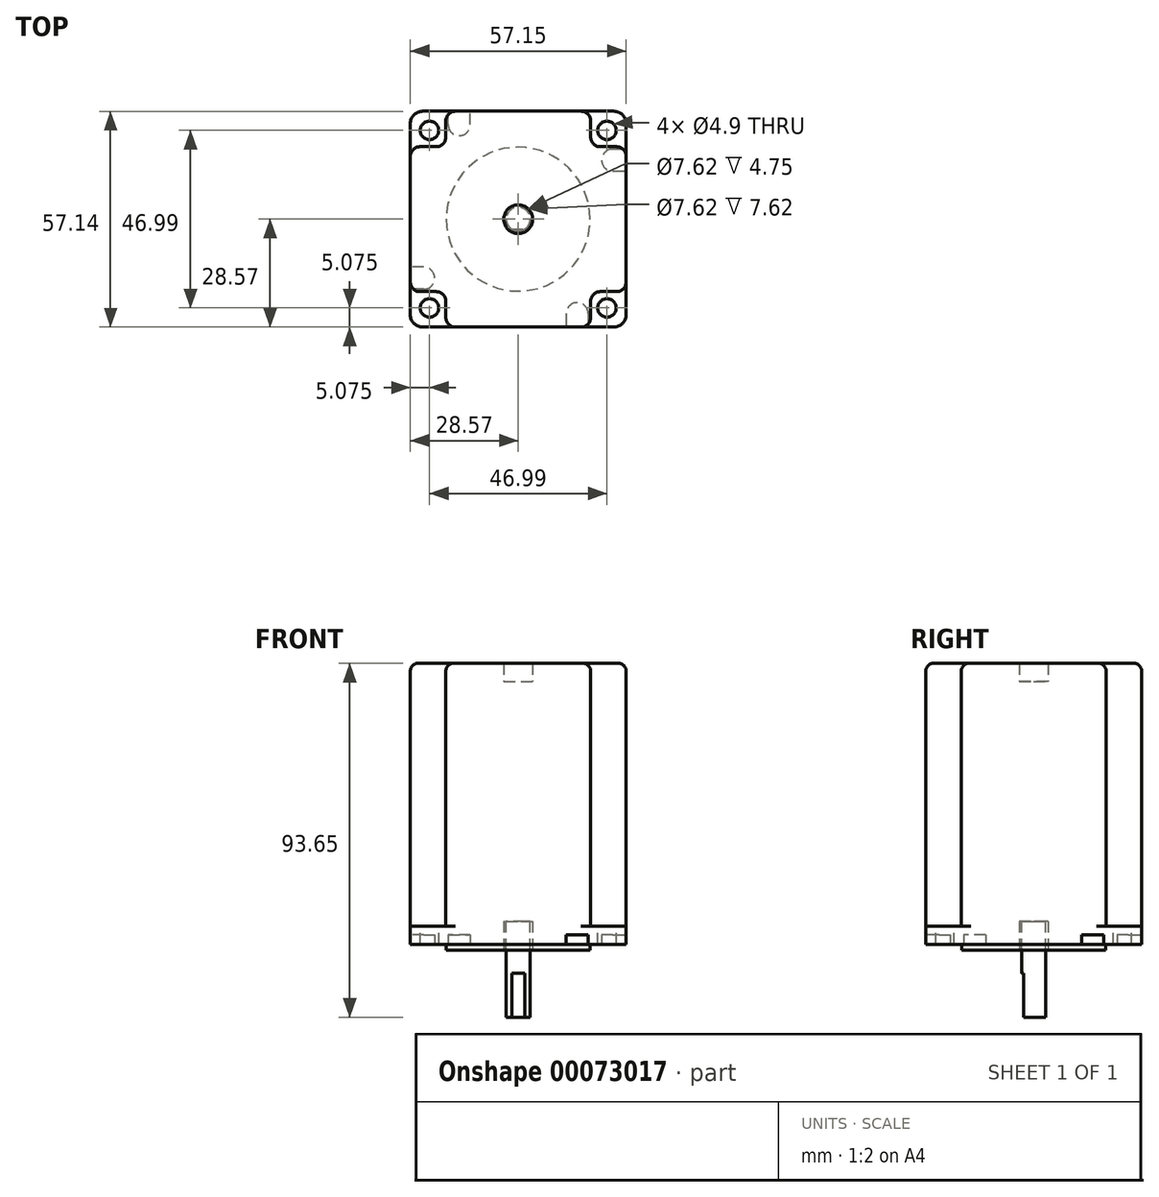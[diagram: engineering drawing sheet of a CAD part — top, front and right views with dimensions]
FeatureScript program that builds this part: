
annotation { "Feature Type Name" : "Feature", "Feature Type Description" : "" }
export const myFeature = defineFeature(function(context is Context, id is Id, definition is map)
    precondition{}
    {
        {
            var Q0;
            Q0=qCreatedBy(makeId("Top.planeOp"),FACE);
            var sketch = newSketch(context, id + "F0", { "sketchPlane" : qUnion([Q0])});
            skLineSegment(sketch, "E0.bottom", {"start": v(-25.27, 28.58) * mm, "end": v(25.27, 28.58) * mm});
            skLineSegment(sketch, "E0.top", {"start": v(-25.27, -28.58) * mm, "end": v(25.27, -28.58) * mm});
            skLineSegment(sketch, "E0.left", {"start": v(-28.57, 25.27) * mm, "end": v(-28.58, -25.27) * mm});
            skLineSegment(sketch, "E0.right", {"start": v(28.58, 25.27) * mm, "end": v(28.57, -25.27) * mm});
            skPoint(sketch, "E0.middle", {"position": v(0, 0) * mm});
            skCircle(sketch, "E1", {"center": v(-23.5, 23.5) * mm, "radius": 2.45 * mm});
            skPoint(sketch, "E2.visualSharp", {"position": v(-28.57, 28.58) * mm});
            skArc(sketch, "E2.filletArc", {"start": v(-25.27, 28.58) * mm, "mid": v(-27.6, 27.6) * mm, "end": v(-28.57, 25.27) * mm});
            skPoint(sketch, "E3.visualSharp", {"position": v(28.58, 28.58) * mm});
            skArc(sketch, "E3.filletArc", {"start": v(28.58, 25.27) * mm, "mid": v(27.6, 27.6) * mm, "end": v(25.27, 28.58) * mm});
            skPoint(sketch, "E4.visualSharp", {"position": v(28.57, -28.58) * mm});
            skArc(sketch, "E4.filletArc", {"start": v(25.27, -28.58) * mm, "mid": v(27.6, -27.6) * mm, "end": v(28.57, -25.27) * mm});
            skPoint(sketch, "E5.visualSharp", {"position": v(-28.58, -28.58) * mm});
            skArc(sketch, "E5.filletArc", {"start": v(-28.58, -25.27) * mm, "mid": v(-27.6, -27.6) * mm, "end": v(-25.27, -28.58) * mm});
            skLineSegment(sketch, "E6", {"start": v(0, -6.35) * mm, "end": v(0, 4.8) * mm});
            skLineSegment(sketch, "E7", {"start": v(10.67, 0) * mm, "end": v(-5.7, 0) * mm});
            skCircle(sketch, "E8.MirrorC", {"center": v(23.5, 23.5) * mm, "radius": 2.45 * mm});
            skCircle(sketch, "E9.MirrorC", {"center": v(23.5, -23.5) * mm, "radius": 2.45 * mm});
            skCircle(sketch, "E10.MirrorC", {"center": v(-23.5, -23.5) * mm, "radius": 2.45 * mm});
            skSolve(sketch);
        }
        {
            var Q0;
            Q0 = qSketchRegion(id + "F0", true);
            extrude(context, id + "F1", {"entities" : qUnion([Q0]), "oppositeDirection" : true, "depth" : 4.72 * mm});
        }
        {
            var Q0;
            Q0=makeQuery(id+"F1.opExtrude","CAP_FACE",FACE,{"disambiguationData":[OSD([sQuery(id+"F0.wireOp",EDGE,"E0.bottom"),sQuery(id+"F0.wireOp",EDGE,"E0.top"),sQuery(id+"F0.wireOp",EDGE,"E0.left"),sQuery(id+"F0.wireOp",EDGE,"E0.right"),sQuery(id+"F0.wireOp",EDGE,"E1"),sQuery(id+"F0.wireOp",EDGE,"E2.filletArc"),sQuery(id+"F0.wireOp",EDGE,"E3.filletArc"),sQuery(id+"F0.wireOp",EDGE,"E4.filletArc"),sQuery(id+"F0.wireOp",EDGE,"E5.filletArc"),sQuery(id+"F0.wireOp",EDGE,"E8.MirrorC"),sQuery(id+"F0.wireOp",EDGE,"E9.MirrorC"),sQuery(id+"F0.wireOp",EDGE,"E10.MirrorC")])],"isStart":false});
            var sketch = newSketch(context, id + "F2", { "sketchPlane" : qUnion([Q0])});
            skCircle(sketch, "E11", {"center": v(0, 0) * mm, "radius": 19.05 * mm});
            skSolve(sketch);
        }
        {
            var Q0;
            Q0 = qSketchRegion(id + "F2", true);
            extrude(context, id + "F3", {"entities" : qUnion([Q0]), "operationType" : NewBodyOperationType.ADD, "depth" : 1.52 * mm});
        }
        {
            var Q0;
            Q0=makeQuery(id+"F1.opExtrude","CAP_FACE",FACE,{"disambiguationData":[OSD([sQuery(id+"F0.wireOp",EDGE,"E0.bottom"),sQuery(id+"F0.wireOp",EDGE,"E0.top"),sQuery(id+"F0.wireOp",EDGE,"E0.left"),sQuery(id+"F0.wireOp",EDGE,"E0.right"),sQuery(id+"F0.wireOp",EDGE,"E1"),sQuery(id+"F0.wireOp",EDGE,"E2.filletArc"),sQuery(id+"F0.wireOp",EDGE,"E3.filletArc"),sQuery(id+"F0.wireOp",EDGE,"E4.filletArc"),sQuery(id+"F0.wireOp",EDGE,"E5.filletArc"),sQuery(id+"F0.wireOp",EDGE,"E8.MirrorC"),sQuery(id+"F0.wireOp",EDGE,"E9.MirrorC"),sQuery(id+"F0.wireOp",EDGE,"E10.MirrorC")])],"isStart":false});
            var sketch = newSketch(context, id + "F4", { "sketchPlane" : qUnion([Q0])});
            skLineSegment(sketch, "E12", {"start": v(7.64, 0) * mm, "end": v(-5.07, 0) * mm});
            skLineSegment(sketch, "E13", {"start": v(0, 10.95) * mm, "end": v(0, -5.13) * mm});
            skArc(sketch, "E14", {"start": v(-25.02, 12.7) * mm, "mid": v(-22.1, 15.62) * mm, "end": v(-25.02, 18.54) * mm});
            skLineSegment(sketch, "E15", {"start": v(-25.02, 12.7) * mm, "end": v(-28.58, 12.7) * mm});
            skLineSegment(sketch, "E16", {"start": v(-25.02, 18.54) * mm, "end": v(-28.58, 18.54) * mm});
            skLineSegment(sketch, "E17", {"start": v(-28.58, 18.54) * mm, "end": v(-28.58, 12.7) * mm});
            skLineSegment(sketch, "E18.MirrorCS", {"start": v(25.02, -12.7) * mm, "end": v(28.58, -12.7) * mm});
            skArc(sketch, "E19.MirrorCS", {"start": v(25.02, -12.7) * mm, "mid": v(22.1, -15.62) * mm, "end": v(25.02, -18.54) * mm});
            skLineSegment(sketch, "E20.MirrorCS", {"start": v(28.58, -18.54) * mm, "end": v(28.58, -12.7) * mm});
            skLineSegment(sketch, "E21.MirrorCS", {"start": v(25.02, -18.54) * mm, "end": v(28.58, -18.54) * mm});
            skArc(sketch, "E22", {"start": v(12.7, 25.02) * mm, "mid": v(15.62, 22.1) * mm, "end": v(18.54, 25.02) * mm});
            skLineSegment(sketch, "E23", {"start": v(12.7, 25.02) * mm, "end": v(12.7, 28.58) * mm});
            skLineSegment(sketch, "E24", {"start": v(18.54, 25.02) * mm, "end": v(18.54, 28.58) * mm});
            skLineSegment(sketch, "E25", {"start": v(18.54, 28.58) * mm, "end": v(12.7, 28.58) * mm});
            skLineSegment(sketch, "E26.MirrorCS", {"start": v(-18.54, -25.02) * mm, "end": v(-18.54, -28.58) * mm});
            skLineSegment(sketch, "E27.MirrorCS", {"start": v(-12.7, -25.02) * mm, "end": v(-12.7, -28.58) * mm});
            skLineSegment(sketch, "E28.MirrorCS", {"start": v(-18.54, -28.58) * mm, "end": v(-12.7, -28.58) * mm});
            skArc(sketch, "E29.MirrorCS", {"start": v(-12.7, -25.02) * mm, "mid": v(-15.62, -22.1) * mm, "end": v(-18.54, -25.02) * mm});
            skSolve(sketch);
        }
        {
            var Q0;
            Q0 = qSketchRegion(id + "F4", true);
            extrude(context, id + "F5", {"entities" : qUnion([Q0]), "operationType" : NewBodyOperationType.REMOVE, "oppositeDirection" : true, "depth" : 2.54 * mm});
        }
        {
            var Q0;
            Q0=makeQuery(id+"F1.opExtrude","CAP_FACE",FACE,{"disambiguationData":[OSD([sQuery(id+"F0.wireOp",EDGE,"E0.bottom"),sQuery(id+"F0.wireOp",EDGE,"E0.top"),sQuery(id+"F0.wireOp",EDGE,"E0.left"),sQuery(id+"F0.wireOp",EDGE,"E0.right"),sQuery(id+"F0.wireOp",EDGE,"E1"),sQuery(id+"F0.wireOp",EDGE,"E2.filletArc"),sQuery(id+"F0.wireOp",EDGE,"E3.filletArc"),sQuery(id+"F0.wireOp",EDGE,"E4.filletArc"),sQuery(id+"F0.wireOp",EDGE,"E5.filletArc"),sQuery(id+"F0.wireOp",EDGE,"E8.MirrorC"),sQuery(id+"F0.wireOp",EDGE,"E9.MirrorC"),sQuery(id+"F0.wireOp",EDGE,"E10.MirrorC")])],"isStart":true});
            var sketch = newSketch(context, id + "F6", { "sketchPlane" : qUnion([Q0])});
            skLineSegment(sketch, "E30", {"start": v(-26.04, 19.18) * mm, "end": v(-21.72, 19.18) * mm});
            skLineSegment(sketch, "E31", {"start": v(-19.18, 21.72) * mm, "end": v(-19.18, 26.04) * mm});
            skLineSegment(sketch, "E32", {"start": v(-16.64, 28.58) * mm, "end": v(16.64, 28.58) * mm});
            skLineSegment(sketch, "E33", {"start": v(19.18, 26.04) * mm, "end": v(19.18, 21.72) * mm});
            skLineSegment(sketch, "E34", {"start": v(21.72, 19.18) * mm, "end": v(26.04, 19.18) * mm});
            skPoint(sketch, "E35.endSnap0", {"position": v(-28.58, 0) * mm});
            skPoint(sketch, "E36.visualSharp", {"position": v(-19.18, 19.18) * mm});
            skArc(sketch, "E36.filletArc", {"start": v(-21.72, 19.18) * mm, "mid": v(-19.92, 19.92) * mm, "end": v(-19.18, 21.72) * mm});
            skPoint(sketch, "E37.visualSharp", {"position": v(19.18, 19.18) * mm});
            skArc(sketch, "E37.filletArc", {"start": v(19.18, 21.72) * mm, "mid": v(19.92, 19.92) * mm, "end": v(21.72, 19.18) * mm});
            skPoint(sketch, "E38.visualSharp", {"position": v(-19.18, 28.58) * mm});
            skArc(sketch, "E38.filletArc", {"start": v(-16.64, 28.58) * mm, "mid": v(-18.43, 27.83) * mm, "end": v(-19.18, 26.04) * mm});
            skPoint(sketch, "E39.visualSharp", {"position": v(19.18, 28.58) * mm});
            skArc(sketch, "E39.filletArc", {"start": v(19.18, 26.04) * mm, "mid": v(18.43, 27.83) * mm, "end": v(16.64, 28.58) * mm});
            skLineSegment(sketch, "E40", {"start": v(-28.58, 16.64) * mm, "end": v(-28.58, 0) * mm});
            skLineSegment(sketch, "E41", {"start": v(28.58, 16.64) * mm, "end": v(28.58, 0) * mm});
            skPoint(sketch, "E42.visualSharp", {"position": v(-28.58, 19.18) * mm});
            skArc(sketch, "E42.filletArc", {"start": v(-26.04, 19.18) * mm, "mid": v(-27.83, 18.43) * mm, "end": v(-28.58, 16.64) * mm});
            skPoint(sketch, "E43.visualSharp", {"position": v(28.58, 19.18) * mm});
            skArc(sketch, "E43.filletArc", {"start": v(28.58, 16.64) * mm, "mid": v(27.83, 18.43) * mm, "end": v(26.04, 19.18) * mm});
            skLineSegment(sketch, "E44", {"start": v(0, 0) * mm, "end": v(13.29, 0) * mm});
            skArc(sketch, "E45.MirrorCS", {"start": v(-16.64, -28.58) * mm, "mid": v(-18.43, -27.83) * mm, "end": v(-19.18, -26.04) * mm});
            skArc(sketch, "E46.MirrorCS", {"start": v(19.18, -26.04) * mm, "mid": v(18.43, -27.83) * mm, "end": v(16.64, -28.58) * mm});
            skArc(sketch, "E47.MirrorCS", {"start": v(28.58, -16.64) * mm, "mid": v(27.83, -18.43) * mm, "end": v(26.04, -19.18) * mm});
            skArc(sketch, "E48.MirrorCS", {"start": v(19.18, -21.72) * mm, "mid": v(19.92, -19.92) * mm, "end": v(21.72, -19.18) * mm});
            skArc(sketch, "E49.MirrorCS", {"start": v(-21.72, -19.18) * mm, "mid": v(-19.92, -19.92) * mm, "end": v(-19.18, -21.72) * mm});
            skArc(sketch, "E50.MirrorCS", {"start": v(-26.04, -19.18) * mm, "mid": v(-27.83, -18.43) * mm, "end": v(-28.58, -16.64) * mm});
            skPoint(sketch, "E51.MirrorP", {"position": v(19.18, -19.18) * mm});
            skLineSegment(sketch, "E52.MirrorCS", {"start": v(-26.04, -19.18) * mm, "end": v(-21.72, -19.18) * mm});
            skPoint(sketch, "E53.MirrorP", {"position": v(-19.18, -19.18) * mm});
            skLineSegment(sketch, "E54.MirrorCS", {"start": v(-28.58, -16.64) * mm, "end": v(-28.58, 0) * mm});
            skPoint(sketch, "E55.MirrorP", {"position": v(28.58, -19.18) * mm});
            skLineSegment(sketch, "E56.MirrorCS", {"start": v(-19.18, -21.72) * mm, "end": v(-19.18, -26.04) * mm});
            skLineSegment(sketch, "E57.MirrorCS", {"start": v(21.72, -19.18) * mm, "end": v(26.04, -19.18) * mm});
            skPoint(sketch, "E58.MirrorP", {"position": v(19.18, -28.58) * mm});
            skLineSegment(sketch, "E59.MirrorCS", {"start": v(-16.64, -28.58) * mm, "end": v(16.64, -28.58) * mm});
            skLineSegment(sketch, "E60.MirrorCS", {"start": v(28.58, -16.64) * mm, "end": v(28.58, 0) * mm});
            skPoint(sketch, "E61.MirrorP", {"position": v(-19.18, -28.58) * mm});
            skPoint(sketch, "E62.MirrorP", {"position": v(-28.58, -19.18) * mm});
            skLineSegment(sketch, "E63.MirrorCS", {"start": v(19.18, -26.04) * mm, "end": v(19.18, -21.72) * mm});
            skSolve(sketch);
        }
        {
            var Q0;
            Q0 = qSketchRegion(id + "F6", true);
            extrude(context, id + "F7", {"entities" : qUnion([Q0]), "operationType" : NewBodyOperationType.ADD, "depth" : 5.84 * mm});
        }
        {
            var Q0;
            Q0=makeQuery(id+"F7.opExtrude","CAP_FACE",FACE,{"disambiguationData":[OSD([sQuery(id+"F6.wireOp",EDGE,"E30"),sQuery(id+"F6.wireOp",EDGE,"E31"),sQuery(id+"F6.wireOp",EDGE,"E32"),sQuery(id+"F6.wireOp",EDGE,"E33"),sQuery(id+"F6.wireOp",EDGE,"E34"),sQuery(id+"F6.wireOp",EDGE,"E36.filletArc"),sQuery(id+"F6.wireOp",EDGE,"E37.filletArc"),sQuery(id+"F6.wireOp",EDGE,"E38.filletArc"),sQuery(id+"F6.wireOp",EDGE,"E39.filletArc"),sQuery(id+"F6.wireOp",EDGE,"E40"),sQuery(id+"F6.wireOp",EDGE,"E41"),sQuery(id+"F6.wireOp",EDGE,"E42.filletArc"),sQuery(id+"F6.wireOp",EDGE,"E43.filletArc"),sQuery(id+"F6.wireOp",EDGE,"E45.MirrorCS"),sQuery(id+"F6.wireOp",EDGE,"E46.MirrorCS"),sQuery(id+"F6.wireOp",EDGE,"E47.MirrorCS"),sQuery(id+"F6.wireOp",EDGE,"E48.MirrorCS"),sQuery(id+"F6.wireOp",EDGE,"E49.MirrorCS"),sQuery(id+"F6.wireOp",EDGE,"E50.MirrorCS"),sQuery(id+"F6.wireOp",EDGE,"E52.MirrorCS"),sQuery(id+"F6.wireOp",EDGE,"E54.MirrorCS"),sQuery(id+"F6.wireOp",EDGE,"E56.MirrorCS"),sQuery(id+"F6.wireOp",EDGE,"E57.MirrorCS"),sQuery(id+"F6.wireOp",EDGE,"E59.MirrorCS"),sQuery(id+"F6.wireOp",EDGE,"E60.MirrorCS"),sQuery(id+"F6.wireOp",EDGE,"E63.MirrorCS")])],"isStart":false});
            extrude(context, id + "F8", {"entities" : qUnion([Q0]), "operationType" : NewBodyOperationType.ADD, "depth" : 52.98 * mm});
        }
        {
            var Q0;
            Q0=makeQuery(id+"F8.opExtrude","CAP_FACE",FACE,{"disambiguationData":[OSD([sQuery(id+"F6.wireOp",EDGE,"E30"),sQuery(id+"F6.wireOp",EDGE,"E31"),sQuery(id+"F6.wireOp",EDGE,"E32"),sQuery(id+"F6.wireOp",EDGE,"E33"),sQuery(id+"F6.wireOp",EDGE,"E34"),sQuery(id+"F6.wireOp",EDGE,"E36.filletArc"),sQuery(id+"F6.wireOp",EDGE,"E37.filletArc"),sQuery(id+"F6.wireOp",EDGE,"E38.filletArc"),sQuery(id+"F6.wireOp",EDGE,"E39.filletArc"),sQuery(id+"F6.wireOp",EDGE,"E40"),sQuery(id+"F6.wireOp",EDGE,"E41"),sQuery(id+"F6.wireOp",EDGE,"E42.filletArc"),sQuery(id+"F6.wireOp",EDGE,"E43.filletArc"),sQuery(id+"F6.wireOp",EDGE,"E45.MirrorCS"),sQuery(id+"F6.wireOp",EDGE,"E46.MirrorCS"),sQuery(id+"F6.wireOp",EDGE,"E47.MirrorCS"),sQuery(id+"F6.wireOp",EDGE,"E48.MirrorCS"),sQuery(id+"F6.wireOp",EDGE,"E49.MirrorCS"),sQuery(id+"F6.wireOp",EDGE,"E50.MirrorCS"),sQuery(id+"F6.wireOp",EDGE,"E52.MirrorCS"),sQuery(id+"F6.wireOp",EDGE,"E54.MirrorCS"),sQuery(id+"F6.wireOp",EDGE,"E56.MirrorCS"),sQuery(id+"F6.wireOp",EDGE,"E57.MirrorCS"),sQuery(id+"F6.wireOp",EDGE,"E59.MirrorCS"),sQuery(id+"F6.wireOp",EDGE,"E60.MirrorCS"),sQuery(id+"F6.wireOp",EDGE,"E63.MirrorCS")])],"isStart":false});
            extrude(context, id + "F9", {"entities" : qUnion([Q0]), "operationType" : NewBodyOperationType.ADD, "depth" : 10.8 * mm});
        }
        {
            var Q0;
            Q0=makeQuery(id+"F9.opExtrude","CAP_EDGE",EDGE,{"disambiguationData":[OSD([sQuery(id+"F6.wireOp",EDGE,"E40"),sQuery(id+"F6.wireOp",EDGE,"E54.MirrorCS")])],"isStart":false});
            fillet(context, id + "F10", {"entities" : qUnion([Q0]), "radius" : 2.03 * mm, "tangentPropagation" : true, "allowEdgeOverflow" : false});
        }
        {
            var Q0;
            Q0=makeQuery(id+"F3.opExtrude","CAP_FACE",FACE,{"disambiguationData":[OSD([sQuery(id+"F2.wireOp",EDGE,"E11")])],"isStart":false});
            var sketch = newSketch(context, id + "F11", { "sketchPlane" : qUnion([Q0])});
            skSolve(sketch);
        }
        {
            var Q0;
            Q0=makeQuery(id+"F11.imprint","IMPRINT",FACE,{"disambiguationData":[TD([[makeQuery(id+"F11.imprint","IMPRINT",EDGE,{"derivedFrom":makeQuery(id+"F3.opExtrude","CAP_EDGE",EDGE,{"disambiguationData":[OSD([sQuery(id+"F2.wireOp",EDGE,"E11")])],"isStart":false})}),1.0]])]});
            var sketch = newSketch(context, id + "F12", { "sketchPlane" : qUnion([Q0])});
            skCircle(sketch, "E64", {"center": v(0, 0) * mm, "radius": 3.81 * mm});
            skSolve(sketch);
        }
        {
            var Q0;
            Q0 = qSketchRegion(id + "F12", true);
            extrude(context, id + "F13", {"entities" : qUnion([Q0]), "operationType" : NewBodyOperationType.REMOVE, "endBound" : BoundingType.UP_TO_NEXT, "oppositeDirection" : true, "depth" : 25.4 * mm});
        }
        {
            var Q0;
            Q0=makeQuery(id+"F11.imprint","IMPRINT",FACE,{"disambiguationData":[TD([[makeQuery(id+"F11.imprint","IMPRINT",EDGE,{"derivedFrom":makeQuery(id+"F3.opExtrude","CAP_EDGE",EDGE,{"disambiguationData":[OSD([sQuery(id+"F2.wireOp",EDGE,"E11")])],"isStart":false})}),1.0]])]});
            var sketch = newSketch(context, id + "F14", { "sketchPlane" : qUnion([Q0])});
            skCircle(sketch, "E65", {"center": v(0, 0) * mm, "radius": 3.81 * mm});
            skSolve(sketch);
        }
        {
            var Q0;
            Q0=makeQuery(id+"F14.imprint","IMPRINT",FACE,{"disambiguationData":[TD([[makeQuery(id+"F14.imprint","IMPRINT",EDGE,{"derivedFrom":sQuery(id+"F14.wireOp",EDGE,"E65")}),-1.0]])]});
            cPlane(context, id + "F15", {"entities" : qUnion([Q0]), "cplaneType" : CPlaneType.OFFSET, "offset" : 7.62 * mm, "oppositeDirection" : true, "width" : 152.4 * mm, "height" : 152.4 * mm});
        }
        {
            var Q0;
            Q0=qCreatedBy(id+"F15.planeOp",FACE);
            var sketch = newSketch(context, id + "F16", { "sketchPlane" : qUnion([Q0])});
            skCircle(sketch, "E66", {"center": v(0, 0) * mm, "radius": 3.81 * mm});
            skSolve(sketch);
        }
        {
            var Q0;
            Q0 = qSketchRegion(id + "F16", true);
            extrude(context, id + "F17", {"entities" : qUnion([Q0]), "operationType" : NewBodyOperationType.ADD, "oppositeDirection" : true, "depth" : 63.5 * mm});
        }
        {
            var Q0;
            Q0=qCreatedBy(id+"F15.planeOp",FACE);
            var sketch = newSketch(context, id + "F18", { "sketchPlane" : qUnion([Q0])});
            skCircle(sketch, "E67", {"center": v(0, 0) * mm, "radius": 3.18 * mm});
            skSolve(sketch);
        }
        {
            var Q0;
            Q0 = qSketchRegion(id + "F18", true);
            extrude(context, id + "F19", {"entities" : qUnion([Q0]), "operationType" : NewBodyOperationType.ADD, "depth" : 25.4 * mm});
        }
        {
            var Q0;
            Q0=makeQuery(id+"F19.opExtrude","CAP_FACE",FACE,{"disambiguationData":[OSD([sQuery(id+"F18.wireOp",EDGE,"E67")])],"isStart":false});
            var sketch = newSketch(context, id + "F20", { "sketchPlane" : qUnion([Q0])});
            skLineSegment(sketch, "E68", {"start": v(-5.7, 2.67) * mm, "end": v(7.14, 2.67) * mm});
            skLineSegment(sketch, "E69.bottom", {"start": v(-5.7, 2.67) * mm, "end": v(7.2, 2.67) * mm});
            skLineSegment(sketch, "E69.top", {"start": v(-5.7, 6.19) * mm, "end": v(7.2, 6.19) * mm});
            skLineSegment(sketch, "E69.left", {"start": v(-5.7, 2.67) * mm, "end": v(-5.7, 6.19) * mm});
            skLineSegment(sketch, "E69.right", {"start": v(7.2, 2.67) * mm, "end": v(7.2, 6.19) * mm});
            skSolve(sketch);
        }
        {
            var Q0;
            Q0 = qSketchRegion(id + "F20", true);
            extrude(context, id + "F21", {"entities" : qUnion([Q0]), "operationType" : NewBodyOperationType.REMOVE, "oppositeDirection" : true, "depth" : 11.58 * mm});
        }
    });
